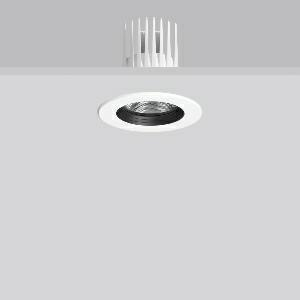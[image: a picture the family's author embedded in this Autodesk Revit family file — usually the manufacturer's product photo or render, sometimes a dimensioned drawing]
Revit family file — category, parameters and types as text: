
# Revit family: heledon_mini_e_901749_002_ec6a
name_source: partatom
category: Lighting Fixtures
units: mm (PartAtom-declared; Revit-internal decimal feet)

## family parameters
Cut with Voids When Loaded = No
Host = Face
Light Source = No
Part Type = Normal
Room Calculation Point = No
Round Connector Dimension = Use Diameter
Shared = No

## types (1)
- HELEDON mini E (1 x LED Modul 930, 3500 lm, 3000)
    Apparent Load = 29 VA
    Approval mark = CE
    CIE Flux Codes = 99 100 100 100 100
    Color Rendering = 90
    Color Temperature = 3000
    Default Elevation = 1800 mm
    Description = Series: HELEDON mini
Round recessed downlight. Housing: die-cast aluminium, powder-coated. Black plastic ring and recessed LED to prevent glare from the side. Optical assembly with reflector made of MIRO-Silver with 98% total light reflection for outstanding efficiency - can be changed without tools. Best colour rendering index Ra>90. Suitable for Recessed ceiling mounting. Installation without tools thanks to spring fastening system. Including separate LED converter with connecting cable 600 mm.High quality converter without flickering and stroboscopic effect. Through-wiring box (5 pole) available as accessory. The following accessories can be mounted without use of tools: interchangeable lenses, decorative glasses, honeycomb louvre, clear and frosted diffusers, white interchangeable plastic ring. 
Colour: traffic white, matt (RAL 9016)
Diameter: 124 mm
Height: 3 mm
Cut-out diameter: 114 mm
Recess height: 170 mm
Luminaire: recess height: 120 mm
Lamp: LED
Socket: without socket
Colour temperature: 3000K
Colour rendering index (CRI): 92
System power: 29 W
Rated luminous flux: 3500 lm
Luminous efficiency: 121 lm/W
Control gear: Regulated power supply
Protection class: II
Type of protection: IP 20
    Height = 0 mm  [stored 0 ft]
    Lamp = 1 x LED Modul 930
    Lamp Light Flux = 3500 lm
    Lamp count = 1
    Length = 124 mm  [stored 0.406824 ft]
    Lifetime = 50000 h
    Luminous efficacy = 121 lm/W
    Manufacturer = RZB
    ModVariant = No
    Model = 901749.002
    Mounting Place = Ceiling
    Mounting Type = Recessed
    Number of Poles = 1
    OnlyDefault = Yes
    Power Factor = 1
    Product Name = HELEDON mini E
    Product group = Recessed downlights
    ProductGroupID = 402
    Protection Class = Protection class II
    Protection Degree = IP 20
    RLX_Detail_Level = 1
    RLX_Emergency_Light_Flux = 0 lm
    RLX_Emergency_Type = 0
    RLX_Emergency_Type_DB = No
    RlxData = <blob elided: 126893 chars, md5=9326f65e>
    Socket = socket
    Standby Power = 0 W
    System Light Flux = 3500 lm
    System Power = 29 W
    Type Comments = Product without accessories
    Type Image = 901657.002.jpg
    URL = http://relux.com
    VarID = ---
    Voltage = 230 V
    Voltage Range = 220-240 V
    Weight = 0.00 kg
    Width = 0 mm  [stored 0 ft]

note: [stored X ft] marks values corroborated as IEEE doubles in the binary element streams (Revit-internal decimal feet)

## geometry (parser evidence)
native form markers: Blend x4, Sweep x12
no freeform markers — native parametric forms only
